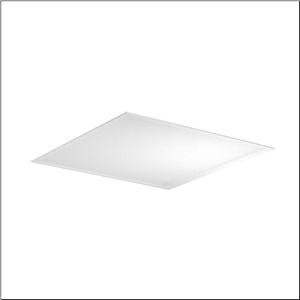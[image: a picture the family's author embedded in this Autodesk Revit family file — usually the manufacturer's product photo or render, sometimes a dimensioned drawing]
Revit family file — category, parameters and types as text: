
# Revit family: apollon_r__31_square_51mp12w72442_a98a
name_source: partatom
category: Lighting Fixtures
units: mm (PartAtom-declared; Revit-internal decimal feet)

## family parameters
Cut with Voids When Loaded = No
Host = Face
Light Source = No
Part Type = Normal
Room Calculation Point = No
Round Connector Dimension = Use Diameter
Shared = No

## types (1)
- Apollon® 31 square (1 x LED, 4000 lm, 27.5 W, 4000K)
    Apparent Load = 28 VA
    CIE Flux Codes = 61 87 97 100 100
    Color Rendering = 80
    Color Temperature = 4000K
    Default Elevation = 1800 mm
    Description = Apollon® 31 square, office luminaire, primary optical cover: micro prismatic cover, of PMMA, CAT 2 (L<= 3000cd/m²), light emission: direct distribution, primary light characteristic: symmetric, installation type: lay-in mounting, LED, rated luminous flux: 4.000lm, luminous efficacy: 145lm/W, light colour: 840, colour temperature: 4000K, with terminal, 3-pole, mains connection: 220..240V, AC, 50/60Hz, rated input power: 28W, housing, of aluminium, traffic white (RAL 9016), module: M600, length: 595mm, width: 595mm, height: 32mm, housing upper side, of sheet steel, galvanised, protection rating (complete): IP20, protection rating (on room side): IP40, insulation class (complete): insulation class II (safety insulation), certification: CE, ENEC, impact resistance: IK03, permissible operating ambient temperature: -20..+40°C, permissible storage temperature: -20..+60°C, packaging unit: 1 piece
    Height = 0 mm  [stored 0 ft]
    Lamp = 1 x LED
    Lamp Light Flux = 4000 lm
    Lamp Power = 27.5 W
    Lamp count = 1
    Length = 595 mm
    Luminous efficacy = 145 lm/W
    Manufacturer = Siteco
    ModVariant = No
    Model = 51MP12W72442
    Mounting Place = Ceiling
    Mounting Type = Recessed
    Number of Poles = 1
    OnlyDefault = Yes
    Power Factor = 1
    Product Name = Apollon® 31 square
    Product group = office luminaire | ceiling recessed
    ProductGroupID = 401
    Protection Class = Protection class II
    Protection Degree = IP 20
    RLX_Detail_Level = 1
    RLX_Emergency_Light_Flux = 0 lm
    RLX_Emergency_Type = 0
    RLX_Emergency_Type_DB = No
    RlxData = <blob elided: 12473 chars, md5=a32048fb>
    Socket = socket
    Standby Power = 0 W
    System Light Flux = 4000 lm
    System Power = 28 W
    Type Comments = Product without accessories
    Type Image = l_1291035.jpg
    URL = http://relux.com
    VarID = ---
    Voltage = 0 V
    Weight = 0.00 kg
    Width = 595 mm

note: [stored X ft] marks values corroborated as IEEE doubles in the binary element streams (Revit-internal decimal feet)

## geometry (parser evidence)
native form markers: Sweep x11
no freeform markers — native parametric forms only
